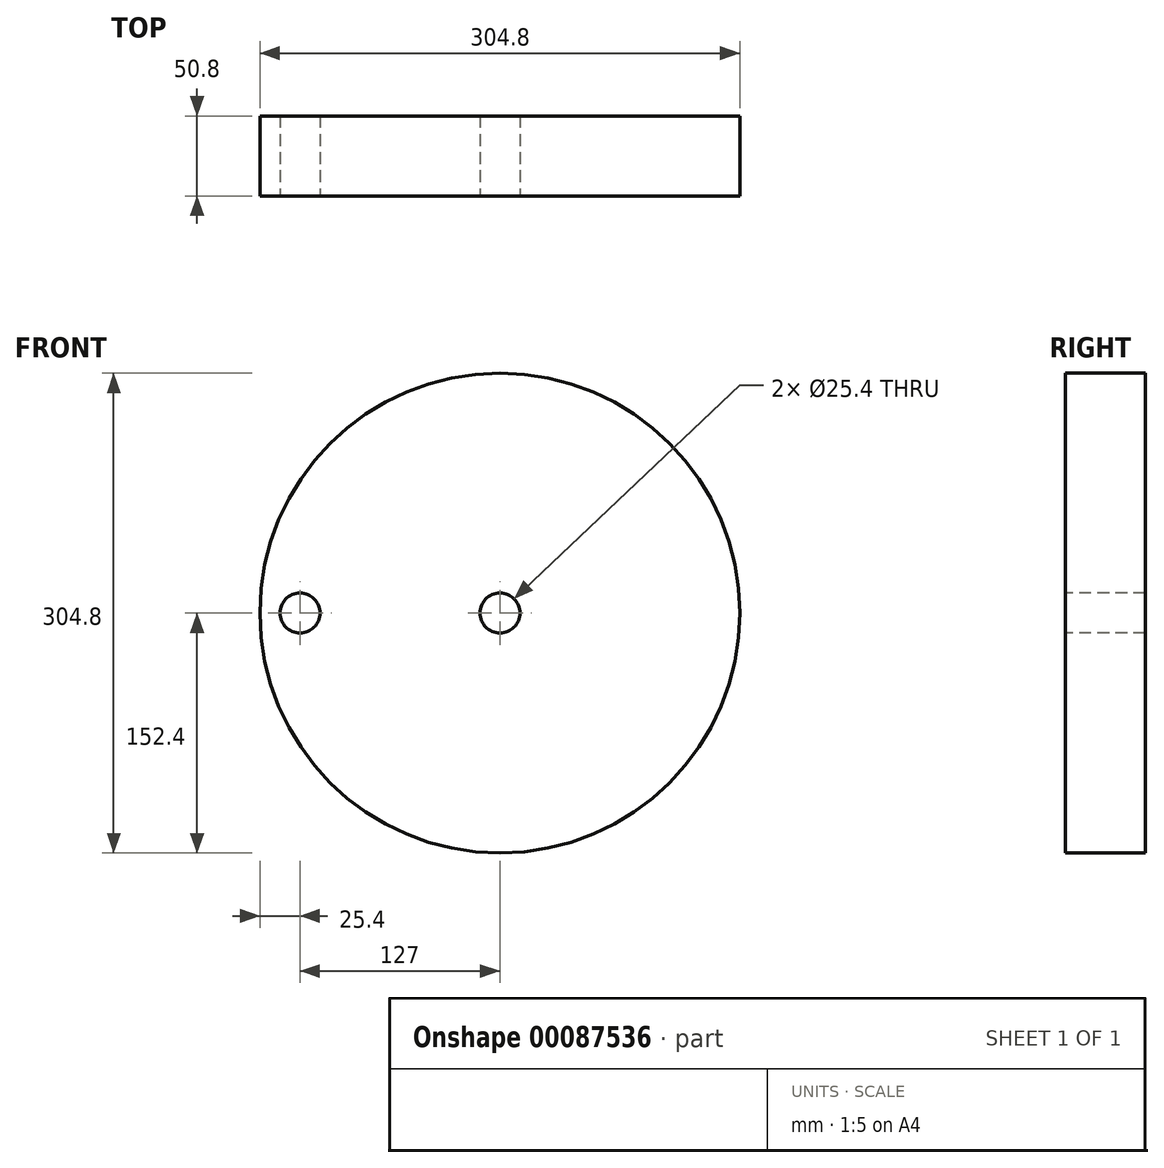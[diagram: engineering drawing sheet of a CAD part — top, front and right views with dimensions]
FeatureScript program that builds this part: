
annotation { "Feature Type Name" : "Feature", "Feature Type Description" : "" }
export const myFeature = defineFeature(function(context is Context, id is Id, definition is map)
    precondition{}
    {
        {
            var Q0;
            Q0=qCreatedBy(makeId("Front.planeOp"),FACE);
            var sketch = newSketch(context, id + "F0", { "sketchPlane" : qUnion([Q0])});
            skCircle(sketch, "E0", {"center": v(0, 0) * mm, "radius": 152.4 * mm});
            skSolve(sketch);
        }
        {
            var Q0;
            Q0=makeQuery(id+"F0.imprint","IMPRINT",FACE,{"disambiguationData":[TD([[makeQuery(id+"F0.imprint","IMPRINT",EDGE,{"derivedFrom":sQuery(id+"F0.wireOp",EDGE,"E0")}),1.0]])]});
            extrude(context, id + "F1", {"entities" : qUnion([Q0]), "depth" : 50.8 * mm});
        }
        {
            var Q0;
            Q0=makeQuery(id+"F1.opExtrude","CAP_FACE",FACE,{"disambiguationData":[OSD([sQuery(id+"F0.wireOp",EDGE,"E0")])],"isStart":false});
            var sketch = newSketch(context, id + "F2", { "sketchPlane" : qUnion([Q0])});
            skCircle(sketch, "E1", {"center": v(-127, 0) * mm, "radius": 12.7 * mm});
            skCircle(sketch, "E2", {"center": v(0, 0) * mm, "radius": 12.7 * mm});
            skCircle(sketch, "E3", {"center": v(0, 0) * mm, "radius": 127 * mm, "construction": true});
            skSolve(sketch);
        }
        {
            var Q0;
            Q0 = qSketchRegion(id + "F2", true);
            extrude(context, id + "F3", {"entities" : qUnion([Q0]), "operationType" : NewBodyOperationType.REMOVE, "endBound" : BoundingType.THROUGH_ALL, "oppositeDirection" : true, "depth" : 25.4 * mm});
        }
    });
